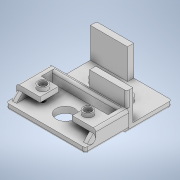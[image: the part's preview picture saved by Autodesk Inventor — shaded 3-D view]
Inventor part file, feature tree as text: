
AUTODESK INVENTOR PART (.ipt)
format: ipt  version: 2020 (Build 240168000, 168)  size: 302,080 bytes
history: native  units: in
note: dims shown in document units (in); Inventor stores cm internally (conversion verified against a paired STEP export)
features: extrude x11, sketch x11, chamfer x3, mirror x1, fillet x1
ambient origin geometry x8: Origin, YZ Plane, XZ Plane, XY Plane, X Axis, Y Axis, Z Axis, Center Point
bodies: Solid1 (feature_tree)
feature tree (27):
  extrude  "Extrusion1"  Depth=1.4331in
  extrude  "Extrusion2"  Depth=1.1811in
  extrude  "Extrusion3"  Depth=1.1811in
  extrude  "Extrusion4"  Depth=0.9606in TaperAngle=0.0deg
  extrude  "Extrusion5"  Depth=0.3406in
  chamfer  "Chamfer1"  Distance=0.1969in
  extrude  "Extrusion6"  Depth=0.1575in
  chamfer  "Chamfer2"  Distance=0.5906in
  extrude  "Extrusion7"  Depth=0.2362in
  extrude  "Extrusion8"  Depth=0.0787in TaperAngle=45.0deg
  mirror  "Mirror1"
  extrude  "Extrusion9"  Depth=0.1969in
  extrude  "Extrusion10"  Depth=0.0787in TaperAngle=45.0deg
  extrude  "Extrusion11"  Depth=0.0787in
  chamfer  "Chamfer3"  Distance=0.1969in
  fillet  "Fillet2"  Radius=0.1181in
  sketch  "Sketch1"  dims[d0=2.3937in d1=1.4331in]
  sketch  "Sketch2"  dims[d2=0.1969in d3=0.0in d4=1.1811in]
  sketch  "Sketch3"  dims[d5=0.1969in d6=1.1811in]
  sketch  "Sketch4"  dims[d7=0.1969in d8=0.9606in d9=0.0in]
  sketch  "Sketch5"  dims[d10=0.3406in d11=0.3406in d12=0.1969in d13=0.0in]
  sketch  "Sketch6"  dims[d14=0.1575in d15=0.1575in d16=0.5906in d17=0.0in]
  sketch  "Sketch7"  dims[d18=0.2362in d19=0.2362in]
  sketch  "Sketch8"  dims[d20=0.1181in d21=0.0in d22=0.0591in d23=0.0787in d24=45.0deg]
  sketch  "Sketch9"  dims[d26=2.5197in d27=0.1969in]
  sketch  "Sketch10"  dims[d28=1.378in d29=0.0in d30=0.1181in d31=0.0787in d32=45.0deg]
  sketch  "Sketch11"  dims[d33=0.1969in d34=1.0492in d35=0.1969in d36=0.1181in d37=0.3543in d38=0.0in d39=0.5906in d40=0.1575in d41=0.5512in d42=0.0in d43=0.315in d44=0.315in d45=0.1181in d46=0.0in d47=0.5906in d48=0.1575in d49=0.1575in d50=1.9685in d51=0.0in d52=0.2362in d53=0.2362in d54=0.1181in d55=0.0in d56=0.1969in d57=0.0787in d58=45.0deg d59=0.0787in]
